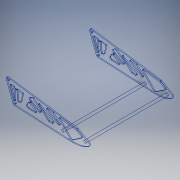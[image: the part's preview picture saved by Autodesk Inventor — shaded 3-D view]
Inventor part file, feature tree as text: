
AUTODESK INVENTOR PART (.ipt)
format: ipt  version: 2018.2 (Build 222227000, 227)  size: 1,171,968 bytes
history: native  units: mm
features: other x5, extrude x2, sketch x2, mirror x1
ambient origin geometry x8: Origin, YZ Plane, XZ Plane, XY Plane, X Axis, Y Axis, Z Axis, Center Point
bodies: Body1 (feature_tree)
feature tree (10):
  other  "bracket1.ipt"
  other  "作業平面1"
  mirror  "ミラー1"
  extrude  "押し出し1"  Depth=10.0mm
  extrude  "押し出し2"  Depth=204.0mm
  other  "ソリッド85::bracket1.ipt"
  other  "TaggingFeature1"
  sketch  "スケッチ1"
  sketch  "スケッチ2"
  other  "ソリッド1"
